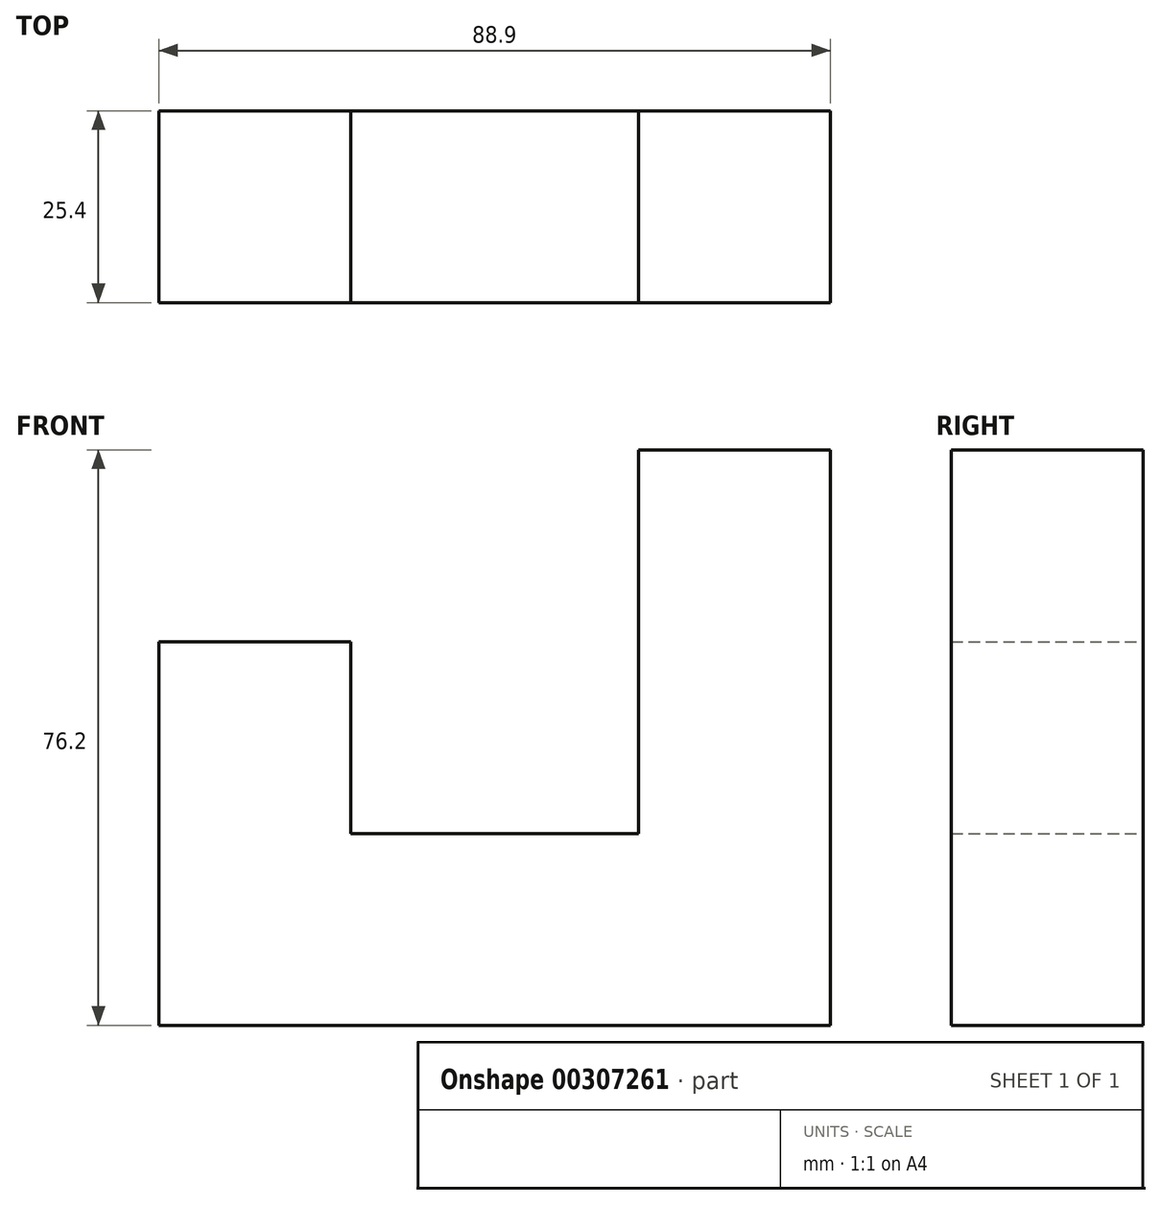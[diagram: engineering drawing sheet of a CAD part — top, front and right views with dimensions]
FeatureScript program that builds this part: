
annotation { "Feature Type Name" : "Feature", "Feature Type Description" : "" }
export const myFeature = defineFeature(function(context is Context, id is Id, definition is map)
    precondition{}
    {
        {
            var Q0;
            Q0=qCreatedBy(makeId("Front.planeOp"),FACE);
            var sketch = newSketch(context, id + "F0", { "sketchPlane" : qUnion([Q0])});
            skLineSegment(sketch, "E0", {"start": v(-45.23, -42.14) * mm, "end": v(43.67, -42.14) * mm});
            skLineSegment(sketch, "E1", {"start": v(43.67, -42.14) * mm, "end": v(43.67, 34.06) * mm});
            skLineSegment(sketch, "E2", {"start": v(43.67, 34.06) * mm, "end": v(18.27, 34.06) * mm});
            skLineSegment(sketch, "E3", {"start": v(18.27, 34.06) * mm, "end": v(18.27, -16.74) * mm});
            skLineSegment(sketch, "E4", {"start": v(18.27, -16.74) * mm, "end": v(-19.83, -16.74) * mm});
            skLineSegment(sketch, "E5", {"start": v(-19.83, -16.74) * mm, "end": v(-19.83, 8.66) * mm});
            skLineSegment(sketch, "E6", {"start": v(-19.83, 8.66) * mm, "end": v(-45.23, 8.66) * mm});
            skLineSegment(sketch, "E7", {"start": v(-45.23, 8.66) * mm, "end": v(-45.23, -42.14) * mm});
            skSolve(sketch);
        }
        {
            var Q0;
            Q0=makeQuery(id+"F0.imprint","IMPRINT",FACE,{"disambiguationData":[TD([[makeQuery(id+"F0.imprint","IMPRINT",EDGE,{"derivedFrom":sQuery(id+"F0.wireOp",EDGE,"E0")}),1.0]])]});
            extrude(context, id + "F1", {"entities" : qUnion([Q0]), "depth" : 25.4 * mm});
        }
    });
